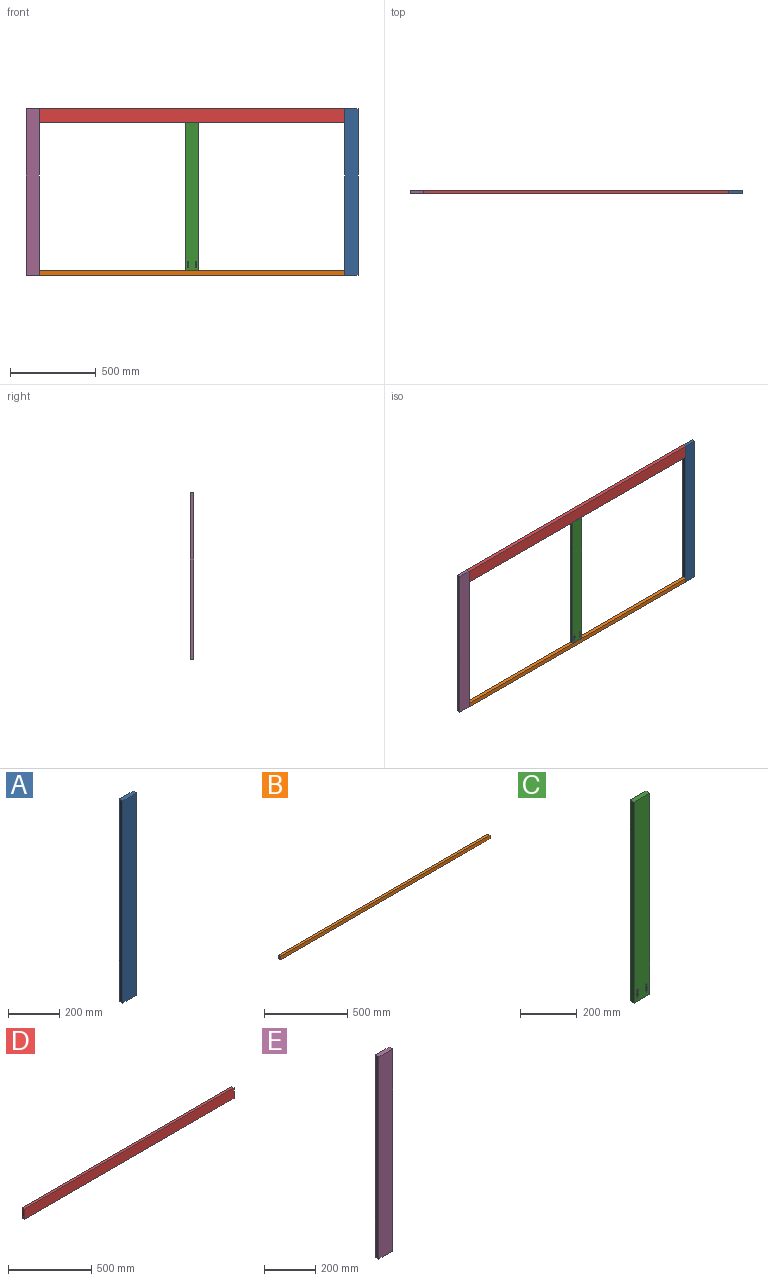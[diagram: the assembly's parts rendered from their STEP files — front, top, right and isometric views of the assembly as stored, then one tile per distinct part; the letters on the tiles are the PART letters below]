
ASSEMBLY  parts=5 mates=4
PART A: 6 faces, bbox 76.2x19.1x965.2 mm
  f0: plane 965.2x19.05mm, normal (-1,0,0), area 18387.1mm2, adj f1,f3,f4,f5
  f1: plane 76.2x19.05mm, normal (0,0,-1), area 1451.6mm2, adj f0,f2,f4,f5
  f2: plane 965.2x19.05mm, normal (1,0,0), area 18387.1mm2, adj f1,f3,f4,f5
  f3: plane 76.2x19.05mm, normal (0,0,1), area 1451.6mm2, adj f0,f2,f4,f5
  f4: plane 965.2x76.2mm, normal (0,-1,0), area 73548.2mm2, adj f0,f1,f2,f3
  f5: plane 965.2x76.2mm, normal (0,1,0), area 73548.2mm2, adj f0,f1,f2,f3
PART B: 14 faces, bbox 1778x28.3x25.4 mm
  f0: plane 1778x19.05mm, normal (0,0,-1), area 33870.9mm2, adj f1,f3,f4,f5
  f1: plane 25.4x19.05mm, normal (1,0,0), area 483.9mm2, adj f0,f2,f4,f5
  f2: plane 1778x19.05mm, normal (0,0,1), area 33870.9mm2, adj f1,f3,f4,f5
  f3: plane 25.4x19.05mm, normal (-1,0,0), area 483.9mm2, adj f0,f2,f4,f5
  f4: plane 1778x25.4mm, normal (0,-1,0), area 45161.2mm2, adj f0,f1,f2,f3
  f5: plane 1778x25.4mm, normal (0,1,0), area 44610.6mm2, adj f0,f1,f2,f3,f6,f10
  f6: cylinder r=4.76mm len=40.55mm, axis (0.97,-0.26,0), area 640.6mm2, adj f5,f7
  f7: plane 9.53x9.2mm, normal (-0.97,0.26,0), area 58.9mm2, adj f6,f9
  f8: plane 3.97x3.83mm, normal (-0.97,0.26,0), area 12.4mm2, adj f9
  f9: cylinder r=1.98mm len=13.29mm, axis (0.97,-0.26,0), area 158.3mm2, adj f7,f8
  f10: cylinder r=4.76mm len=40.55mm, axis (-0.97,-0.26,0), area 640.6mm2, adj f5,f11
  f11: plane 9.53x9.2mm, normal (0.97,0.26,0), area 58.9mm2, adj f10,f13
  f12: plane 3.97x3.83mm, normal (0.97,0.26,0), area 12.4mm2, adj f13
  f13: cylinder r=1.98mm len=13.29mm, axis (-0.97,-0.26,0), area 158.3mm2, adj f11,f12
PART C: 14 faces, bbox 76.2x28.3x863.6 mm
  f0: plane 863.6x19.05mm, normal (1,0,0), area 16451.6mm2, adj f1,f3,f4,f5
  f1: plane 76.2x19.05mm, normal (0,0,1), area 1451.6mm2, adj f0,f2,f4,f5
  f2: plane 863.6x19.05mm, normal (-1,0,0), area 16451.6mm2, adj f1,f3,f4,f5
  f3: plane 76.2x19.05mm, normal (0,0,-1), area 1451.6mm2, adj f0,f2,f4,f5
  f4: plane 863.6x76.2mm, normal (0,-1,0), area 65255.7mm2, adj f0,f1,f2,f3,f6,f10
  f5: plane 863.6x76.2mm, normal (0,1,0), area 65806.3mm2, adj f0,f1,f2,f3
  f6: cylinder r=4.76mm len=40.55mm, axis (0,0.26,-0.97), area 640.6mm2, adj f4,f7
  f7: plane 9.53x9.2mm, normal (0,-0.26,0.97), area 58.9mm2, adj f6,f9
  f8: plane 3.97x3.83mm, normal (0,-0.26,0.97), area 12.4mm2, adj f9
  f9: cylinder r=1.98mm len=13.29mm, axis (0,0.26,-0.97), area 158.3mm2, adj f7,f8
  f10: cylinder r=4.76mm len=40.55mm, axis (0,0.26,-0.97), area 640.6mm2, adj f4,f11
  f11: plane 9.53x9.2mm, normal (0,-0.26,0.97), area 58.9mm2, adj f10,f13
  f12: plane 3.97x3.83mm, normal (0,-0.26,0.97), area 12.4mm2, adj f13
  f13: cylinder r=1.98mm len=13.29mm, axis (0,0.26,-0.97), area 158.3mm2, adj f11,f12
PART D: 22 faces, bbox 1778x28.3x76.2 mm
  f0: plane 1778x19.05mm, normal (0,0,-1), area 33870.9mm2, adj f1,f3,f4,f5
  f1: plane 76.2x19.05mm, normal (1,0,0), area 1451.6mm2, adj f0,f2,f4,f5
  f2: plane 1778x19.05mm, normal (0,0,1), area 33870.9mm2, adj f1,f3,f4,f5
  f3: plane 76.2x19.05mm, normal (-1,0,0), area 1451.6mm2, adj f0,f2,f4,f5
  f4: plane 1778x76.2mm, normal (0,-1,0), area 135483.6mm2, adj f0,f1,f2,f3
  f5: plane 1778x76.2mm, normal (0,1,0), area 134382.4mm2, adj f0,f1,f2,f3,f6,f10,f14,f18
  f6: cylinder r=4.76mm len=40.55mm, axis (0.97,-0.26,0), area 640.6mm2, adj f5,f7
  f7: plane 9.53x9.2mm, normal (-0.97,0.26,0), area 58.9mm2, adj f6,f9
  f8: plane 3.97x3.83mm, normal (-0.97,0.26,0), area 12.4mm2, adj f9
  f9: cylinder r=1.98mm len=13.29mm, axis (0.97,-0.26,0), area 158.3mm2, adj f7,f8
  f10: cylinder r=4.76mm len=40.55mm, axis (0.97,-0.26,0), area 640.6mm2, adj f5,f11
  f11: plane 9.53x9.2mm, normal (-0.97,0.26,0), area 58.9mm2, adj f10,f13
  f12: plane 3.97x3.83mm, normal (-0.97,0.26,0), area 12.4mm2, adj f13
  f13: cylinder r=1.98mm len=13.29mm, axis (0.97,-0.26,0), area 158.3mm2, adj f11,f12
  f14: cylinder r=4.76mm len=40.55mm, axis (-0.97,-0.26,0), area 640.6mm2, adj f5,f15
  f15: plane 9.53x9.2mm, normal (0.97,0.26,0), area 58.9mm2, adj f14,f17
  f16: plane 3.97x3.83mm, normal (0.97,0.26,0), area 12.4mm2, adj f17
  f17: cylinder r=1.98mm len=13.29mm, axis (-0.97,-0.26,0), area 158.3mm2, adj f15,f16
  f18: cylinder r=4.76mm len=40.55mm, axis (-0.97,-0.26,0), area 640.6mm2, adj f5,f19
  f19: plane 9.53x9.2mm, normal (0.97,0.26,0), area 58.9mm2, adj f18,f21
  f20: plane 3.97x3.83mm, normal (0.97,0.26,0), area 12.4mm2, adj f21
  f21: cylinder r=1.98mm len=13.29mm, axis (-0.97,-0.26,0), area 158.3mm2, adj f19,f20
PART E: 6 faces, bbox 76.2x19.1x965.2 mm
  f0: plane 76.2x19.05mm, normal (0,0,-1), area 1451.6mm2, adj f1,f3,f4,f5
  f1: plane 965.2x19.05mm, normal (1,0,0), area 18387.1mm2, adj f0,f2,f4,f5
  f2: plane 76.2x19.05mm, normal (0,0,1), area 1451.6mm2, adj f1,f3,f4,f5
  f3: plane 965.2x19.05mm, normal (-1,0,0), area 18387.1mm2, adj f0,f2,f4,f5
  f4: plane 965.2x76.2mm, normal (0,-1,0), area 73548.2mm2, adj f0,f1,f2,f3
  f5: plane 965.2x76.2mm, normal (0,1,0), area 73548.2mm2, adj f0,f1,f2,f3
PLACE A t=(-14.28,0,-20.47)mm fixed
PLACE B t=(-52.63,0,-412.33)mm
PLACE C t=(-48.16,0,-35.43)mm
PLACE D t=(-75.63,0,-412.33)mm
PLACE E t=(-69.86,0,-20.47)mm
MATE fastened D.f1 <-> A.f0  axis (1,0,0) through (881.9,-19.05,468.53)mm
MATE fastened D.f4 <-> E.f4  axis (0,-1,0) through (-896.1,-19.05,468.53)mm
MATE fastened A.f4 <-> B.f4  axis (0,-1,0) through (881.9,-19.05,-496.67)mm
MATE fastened D.f4 <-> C.f4  axis (0,-1,0) through (-7.1,-19.05,392.33)mm
